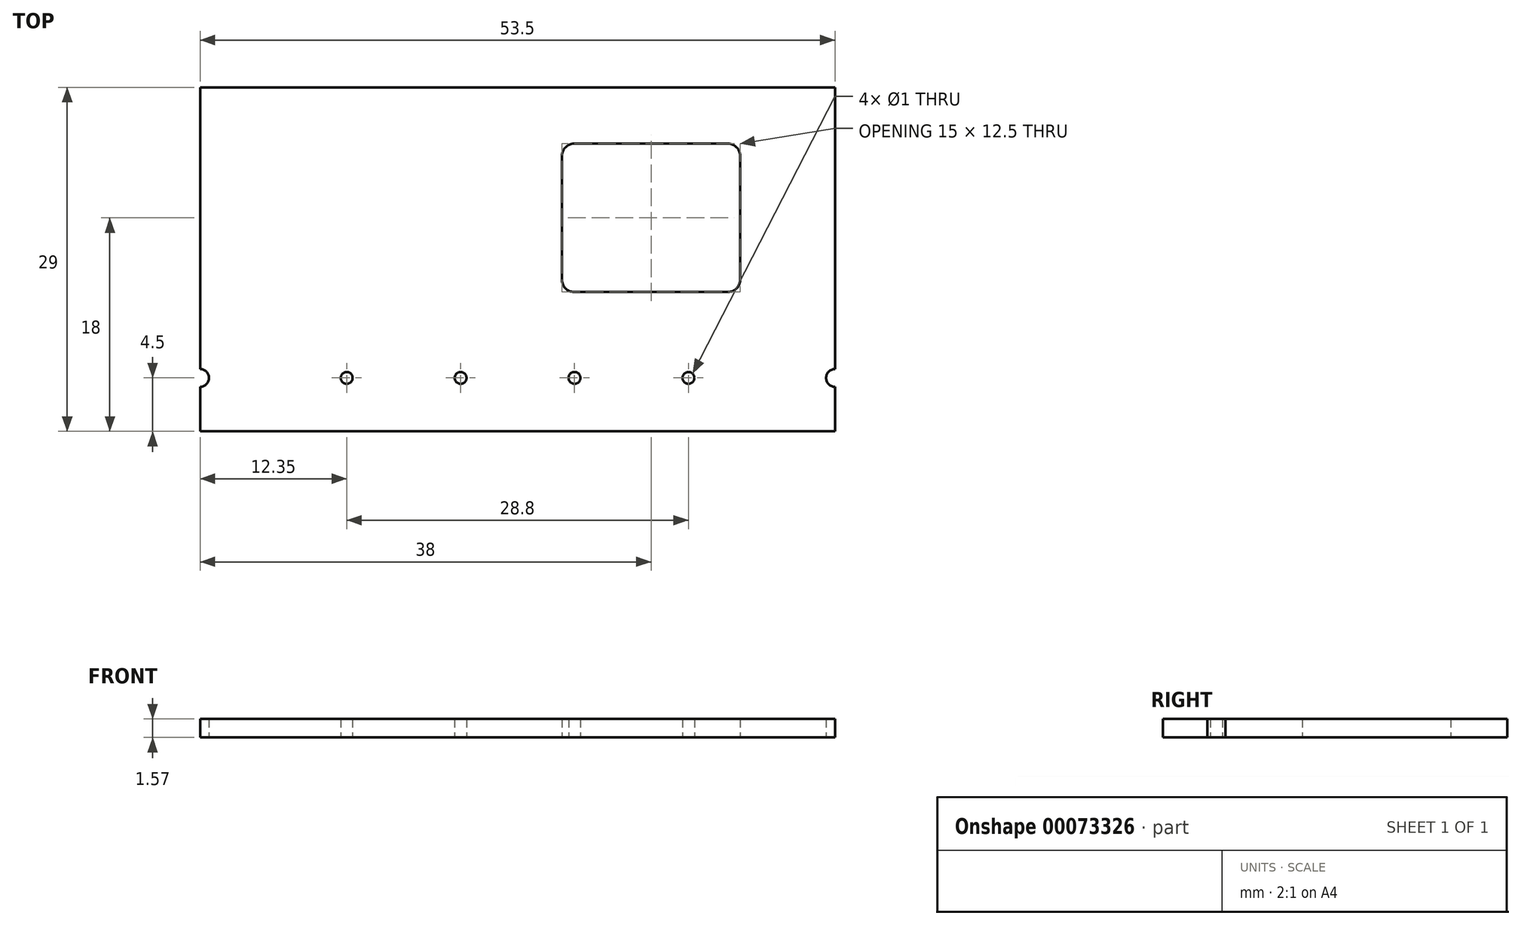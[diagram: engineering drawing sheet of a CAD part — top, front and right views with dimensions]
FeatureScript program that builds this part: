
annotation { "Feature Type Name" : "Feature", "Feature Type Description" : "" }
export const myFeature = defineFeature(function(context is Context, id is Id, definition is map)
    precondition{}
    {
        {
            var Q0;
            Q0=qCreatedBy(makeId("Top.planeOp"),FACE);
            var sketch = newSketch(context, id + "F0", { "sketchPlane" : qUnion([Q0])});
            skPoint(sketch, "E0.middle", {"position": v(0, 0) * mm});
            skLineSegment(sketch, "E1.bottom", {"start": v(4.75, 19.75) * mm, "end": v(17.75, 19.75) * mm});
            skLineSegment(sketch, "E1.top", {"start": v(4.75, 7.25) * mm, "end": v(17.75, 7.25) * mm});
            skLineSegment(sketch, "E1.left", {"start": v(3.75, 18.75) * mm, "end": v(3.75, 8.25) * mm});
            skLineSegment(sketch, "E1.right", {"start": v(18.75, 18.75) * mm, "end": v(18.75, 8.25) * mm});
            skLineSegment(sketch, "E2", {"start": v(-4.8, 0) * mm, "end": v(-14.4, 0) * mm, "construction": true});
            skLineSegment(sketch, "E3", {"start": v(14.4, 0) * mm, "end": v(4.8, 0) * mm, "construction": true});
            skLineSegment(sketch, "E4", {"start": v(4.8, 0) * mm, "end": v(-4.8, 0) * mm, "construction": true});
            skLineSegment(sketch, "E5.bottom", {"start": v(-26.75, -4.5) * mm, "end": v(26.75, -4.5) * mm});
            skLineSegment(sketch, "E5.top", {"start": v(-26.75, 24.5) * mm, "end": v(26.75, 24.5) * mm});
            skLineSegment(sketch, "E5.left", {"start": v(-26.75, -4.5) * mm, "end": v(-26.75, -0.75) * mm});
            skLineSegment(sketch, "E5.right", {"start": v(26.75, -4.5) * mm, "end": v(26.75, -0.75) * mm});
            skPoint(sketch, "E5.middle", {"position": v(0, 10) * mm});
            skCircle(sketch, "E6", {"center": v(-14.4, 0) * mm, "radius": 2.5 * mm, "construction": true});
            skCircle(sketch, "E7", {"center": v(14.4, 0) * mm, "radius": 2.5 * mm, "construction": true});
            skArc(sketch, "E8", {"start": v(26.75, 0.75) * mm, "mid": v(26, 0) * mm, "end": v(26.75, -0.75) * mm});
            skArc(sketch, "E9", {"start": v(-26.75, -0.75) * mm, "mid": v(-26, 0) * mm, "end": v(-26.75, 0.75) * mm});
            skLineSegment(sketch, "E10.trimOffspring", {"start": v(-26.75, 0.75) * mm, "end": v(-26.75, 24.5) * mm});
            skLineSegment(sketch, "E11.trimOffspring", {"start": v(26.75, 0.75) * mm, "end": v(26.75, 24.5) * mm});
            skPoint(sketch, "E12.visualSharp", {"position": v(3.75, 19.75) * mm});
            skArc(sketch, "E12.filletArc", {"start": v(4.75, 19.75) * mm, "mid": v(4.04, 19.46) * mm, "end": v(3.75, 18.75) * mm});
            skPoint(sketch, "E13.visualSharp", {"position": v(3.75, 7.25) * mm});
            skArc(sketch, "E13.filletArc", {"start": v(3.75, 8.25) * mm, "mid": v(4.04, 7.54) * mm, "end": v(4.75, 7.25) * mm});
            skPoint(sketch, "E14.visualSharp", {"position": v(18.75, 7.25) * mm});
            skArc(sketch, "E14.filletArc", {"start": v(17.75, 7.25) * mm, "mid": v(18.46, 7.54) * mm, "end": v(18.75, 8.25) * mm});
            skPoint(sketch, "E15.visualSharp", {"position": v(18.75, 19.75) * mm});
            skArc(sketch, "E15.filletArc", {"start": v(18.75, 18.75) * mm, "mid": v(18.46, 19.46) * mm, "end": v(17.75, 19.75) * mm});
            skLineSegment(sketch, "E16.bottom", {"start": v(-12.85, -1.05) * mm, "end": v(-15.95, -1.05) * mm, "construction": true});
            skLineSegment(sketch, "E16.top", {"start": v(-12.85, 1.05) * mm, "end": v(-15.95, 1.05) * mm, "construction": true});
            skLineSegment(sketch, "E16.left", {"start": v(-12.85, -1.05) * mm, "end": v(-12.85, 1.05) * mm, "construction": true});
            skLineSegment(sketch, "E16.right", {"start": v(-15.95, -1.05) * mm, "end": v(-15.95, 1.05) * mm, "construction": true});
            skLineSegment(sketch, "E17.bottom", {"start": v(-3.25, -1.05) * mm, "end": v(-6.35, -1.05) * mm, "construction": true});
            skLineSegment(sketch, "E17.top", {"start": v(-3.25, 1.05) * mm, "end": v(-6.35, 1.05) * mm, "construction": true});
            skLineSegment(sketch, "E17.left", {"start": v(-3.25, -1.05) * mm, "end": v(-3.25, 1.05) * mm, "construction": true});
            skLineSegment(sketch, "E17.right", {"start": v(-6.35, -1.05) * mm, "end": v(-6.35, 1.05) * mm, "construction": true});
            skPoint(sketch, "E17.middle", {"position": v(-4.8, 0) * mm});
            skLineSegment(sketch, "E18.bottom", {"start": v(6.35, -1.05) * mm, "end": v(3.25, -1.05) * mm, "construction": true});
            skLineSegment(sketch, "E18.top", {"start": v(6.35, 1.05) * mm, "end": v(3.25, 1.05) * mm, "construction": true});
            skLineSegment(sketch, "E18.left", {"start": v(6.35, -1.05) * mm, "end": v(6.35, 1.05) * mm, "construction": true});
            skLineSegment(sketch, "E18.right", {"start": v(3.25, -1.05) * mm, "end": v(3.25, 1.05) * mm, "construction": true});
            skPoint(sketch, "E18.middle", {"position": v(4.8, 0) * mm});
            skLineSegment(sketch, "E19.bottom", {"start": v(15.95, -1.05) * mm, "end": v(12.85, -1.05) * mm, "construction": true});
            skLineSegment(sketch, "E19.top", {"start": v(15.95, 1.05) * mm, "end": v(12.85, 1.05) * mm, "construction": true});
            skLineSegment(sketch, "E19.left", {"start": v(15.95, -1.05) * mm, "end": v(15.95, 1.05) * mm, "construction": true});
            skLineSegment(sketch, "E19.right", {"start": v(12.85, -1.05) * mm, "end": v(12.85, 1.05) * mm, "construction": true});
            skLineSegment(sketch, "E20.bottom", {"start": v(21.75, 4.5) * mm, "end": v(0.75, 4.5) * mm, "construction": true});
            skLineSegment(sketch, "E20.top", {"start": v(21.75, 22.5) * mm, "end": v(0.75, 22.5) * mm, "construction": true});
            skLineSegment(sketch, "E20.left", {"start": v(21.75, 4.5) * mm, "end": v(21.75, 22.5) * mm, "construction": true});
            skLineSegment(sketch, "E20.right", {"start": v(0.75, 4.5) * mm, "end": v(0.75, 22.5) * mm, "construction": true});
            skPoint(sketch, "E20.middle", {"position": v(11.25, 13.5) * mm});
            skPoint(sketch, "E20.middle.positionSnap0", {"position": v(3.75, 13.5) * mm});
            skPoint(sketch, "E20.middle.positionSnap1", {"position": v(11.25, 19.75) * mm});
            skPoint(sketch, "E20.centerSnap0", {"position": v(3.75, 13.5) * mm});
            skPoint(sketch, "E20.centerSnap1", {"position": v(11.25, 19.75) * mm});
            skCircle(sketch, "E21", {"center": v(-14.4, 0) * mm, "radius": 0.5 * mm});
            skCircle(sketch, "E22", {"center": v(-4.8, 0) * mm, "radius": 0.5 * mm});
            skCircle(sketch, "E23", {"center": v(4.8, 0) * mm, "radius": 0.5 * mm});
            skCircle(sketch, "E24", {"center": v(14.4, 0) * mm, "radius": 0.5 * mm});
            skSolve(sketch);
        }
        {
            var Q0;
            Q0 = qSketchRegion(id + "F0", true);
            extrude(context, id + "F1", {"entities" : qUnion([Q0]), "depth" : 1.57 * mm});
        }
    });
